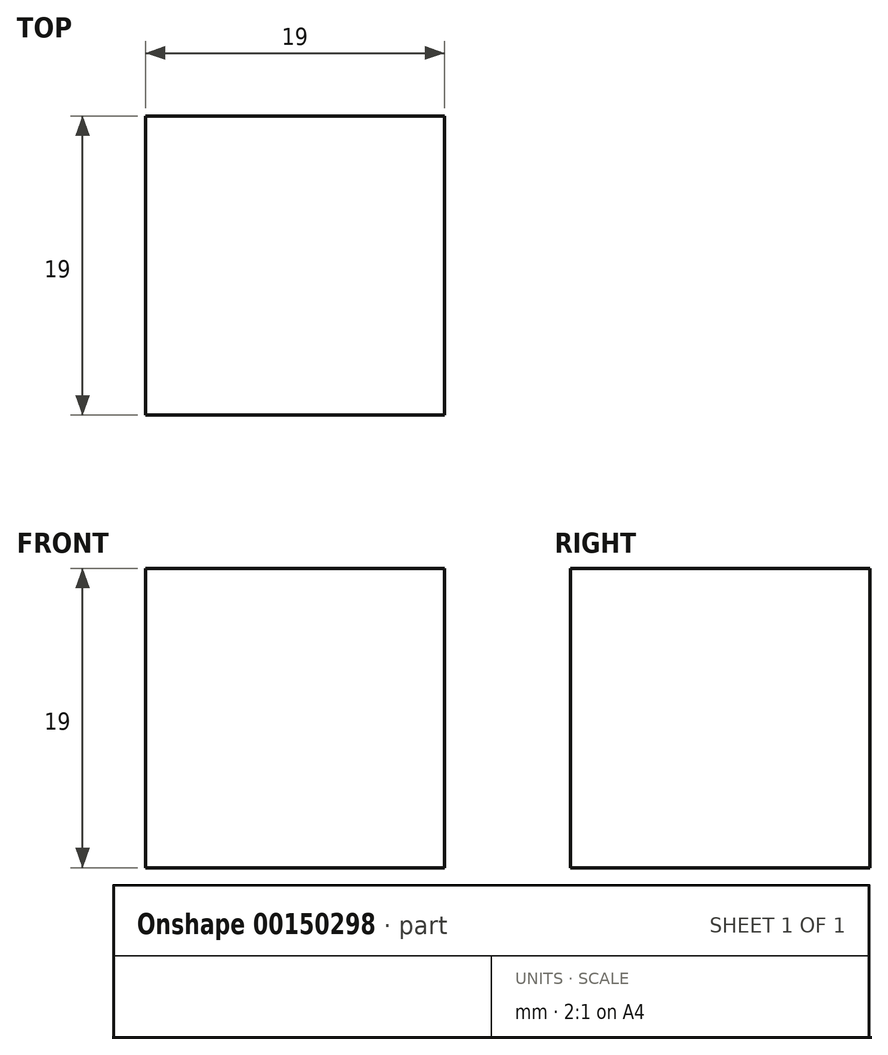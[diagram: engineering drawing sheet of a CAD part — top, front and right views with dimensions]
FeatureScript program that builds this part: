
annotation { "Feature Type Name" : "Feature", "Feature Type Description" : "" }
export const myFeature = defineFeature(function(context is Context, id is Id, definition is map)
    precondition{}
    {
        {
            var Q0;
            Q0=qCreatedBy(makeId("Front.planeOp"),FACE);
            var sketch = newSketch(context, id + "F0", { "sketchPlane" : qUnion([Q0])});
            skLineSegment(sketch, "E0", {"start": v(-60.03, -24.41) * mm, "end": v(-60.03, -43.41) * mm});
            skLineSegment(sketch, "E1", {"start": v(-60.03, -43.41) * mm, "end": v(-41.03, -43.41) * mm});
            skLineSegment(sketch, "E2", {"start": v(-41.03, -43.41) * mm, "end": v(-41.03, -24.41) * mm});
            skLineSegment(sketch, "E3", {"start": v(-41.03, -24.41) * mm, "end": v(-60.03, -24.41) * mm});
            skSolve(sketch);
        }
        {
            var Q0;
            Q0=makeQuery(id+"F0.imprint","IMPRINT",FACE,{"disambiguationData":[TD([[makeQuery(id+"F0.imprint","IMPRINT",EDGE,{"derivedFrom":sQuery(id+"F0.wireOp",EDGE,"E0")}),1.0]])]});
            extrude(context, id + "F1", {"entities" : qUnion([Q0]), "depth" : 19 * mm});
        }
    });
